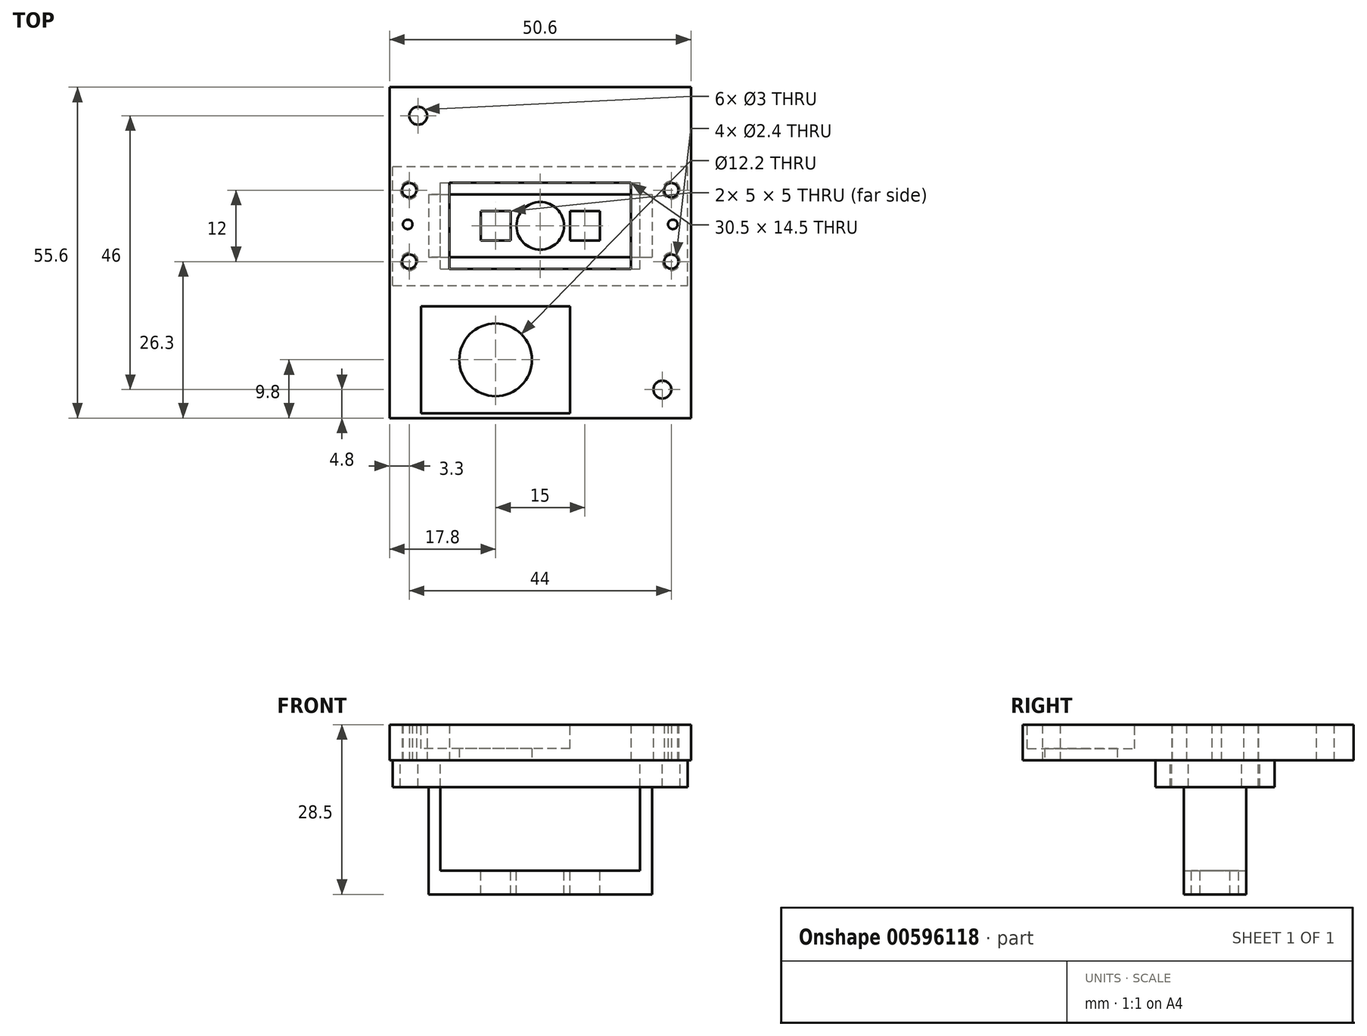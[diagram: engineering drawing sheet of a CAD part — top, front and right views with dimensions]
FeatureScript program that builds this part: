
annotation { "Feature Type Name" : "Feature", "Feature Type Description" : "" }
export const myFeature = defineFeature(function(context is Context, id is Id, definition is map)
    precondition{}
    {
        {
            var Q0;
            Q0=qCreatedBy(makeId("Top.planeOp"),FACE);
            var sketch = newSketch(context, id + "F0", { "sketchPlane" : qUnion([Q0])});
            skLineSegment(sketch, "E0.bottom", {"start": v(25.3, -27.8) * mm, "end": v(-25.3, -27.8) * mm});
            skLineSegment(sketch, "E0.top", {"start": v(25.3, 27.8) * mm, "end": v(-25.3, 27.8) * mm});
            skLineSegment(sketch, "E0.left", {"start": v(25.3, -27.8) * mm, "end": v(25.3, 27.8) * mm});
            skLineSegment(sketch, "E0.right", {"start": v(-25.3, -27.8) * mm, "end": v(-25.3, 27.8) * mm});
            skPoint(sketch, "E0.middle", {"position": v(0, 0) * mm});
            skLineSegment(sketch, "E1.bottom", {"start": v(15.25, -2.75) * mm, "end": v(-15.25, -2.75) * mm});
            skLineSegment(sketch, "E1.top", {"start": v(15.25, 11.75) * mm, "end": v(-15.25, 11.75) * mm});
            skLineSegment(sketch, "E1.left", {"start": v(15.25, -2.75) * mm, "end": v(15.25, 11.75) * mm});
            skLineSegment(sketch, "E1.right", {"start": v(-15.25, -2.75) * mm, "end": v(-15.25, 11.75) * mm});
            skPoint(sketch, "E1.middle", {"position": v(0, 4.5) * mm});
            skCircle(sketch, "E2", {"center": v(-20.5, 23) * mm, "radius": 1.5 * mm});
            skCircle(sketch, "E3", {"center": v(20.5, -23) * mm, "radius": 1.5 * mm});
            skCircle(sketch, "E4", {"center": v(-7.5, -18) * mm, "radius": 6.1 * mm});
            skCircle(sketch, "E5", {"center": v(22.25, 4.75) * mm, "radius": 0.8 * mm});
            skCircle(sketch, "E6", {"center": v(22, 10.5) * mm, "radius": 1.2 * mm});
            skCircle(sketch, "E7", {"center": v(22, -1.5) * mm, "radius": 1.2 * mm});
            skLineSegment(sketch, "E8", {"start": v(0, 4.5) * mm, "end": v(0, 17.43) * mm, "construction": true});
            skCircle(sketch, "E9.MirrorC", {"center": v(-22, -1.5) * mm, "radius": 1.2 * mm});
            skCircle(sketch, "E10.MirrorC", {"center": v(-22.25, 4.75) * mm, "radius": 0.8 * mm});
            skCircle(sketch, "E11.MirrorC", {"center": v(-22, 10.5) * mm, "radius": 1.2 * mm});
            skSolve(sketch);
        }
        {
            var Q0;
            Q0 = qSketchRegion(id + "F0", true);
            extrude(context, id + "F1", {"entities" : qUnion([Q0]), "depth" : 6 * mm, "offsetDistance" : 25 * mm});
        }
        {
            var Q0;
            Q0=makeQuery(id+"F1.opExtrude","CAP_FACE",FACE,{"disambiguationData":[OSD([sQuery(id+"F0.wireOp",EDGE,"E0.bottom"),sQuery(id+"F0.wireOp",EDGE,"E0.top"),sQuery(id+"F0.wireOp",EDGE,"E0.left"),sQuery(id+"F0.wireOp",EDGE,"E0.right"),sQuery(id+"F0.wireOp",EDGE,"E1.bottom"),sQuery(id+"F0.wireOp",EDGE,"E1.top"),sQuery(id+"F0.wireOp",EDGE,"E1.left"),sQuery(id+"F0.wireOp",EDGE,"E1.right"),sQuery(id+"F0.wireOp",EDGE,"E2"),sQuery(id+"F0.wireOp",EDGE,"E3"),sQuery(id+"F0.wireOp",EDGE,"E4"),sQuery(id+"F0.wireOp",EDGE,"vf1jpXBP-j2sW-oR5i-IoB6-HgW2j1TkzSlQ"),sQuery(id+"F0.wireOp",EDGE,"E5")])],"isStart":false});
            var sketch = newSketch(context, id + "F2", { "sketchPlane" : qUnion([Q0])});
            skLineSegment(sketch, "E12.bottom", {"start": v(5, -27) * mm, "end": v(-20, -27) * mm});
            skLineSegment(sketch, "E12.top", {"start": v(5, -9) * mm, "end": v(-20, -9) * mm});
            skLineSegment(sketch, "E12.left", {"start": v(5, -27) * mm, "end": v(5, -9) * mm});
            skLineSegment(sketch, "E12.right", {"start": v(-20, -27) * mm, "end": v(-20, -9) * mm});
            skPoint(sketch, "E12.middle", {"position": v(-7.5, -18) * mm});
            skSolve(sketch);
        }
        {
            var Q0;
            Q0 = qSketchRegion(id + "F2", true);
            extrude(context, id + "F3", {"entities" : qUnion([Q0]), "operationType" : NewBodyOperationType.REMOVE, "oppositeDirection" : true, "depth" : 4 * mm, "offsetDistance" : 25 * mm});
        }
        {
            var Q0;
            Q0=makeQuery(id+"F1.opExtrude","CAP_FACE",FACE,{"disambiguationData":[OSD([sQuery(id+"F0.wireOp",EDGE,"E0.bottom"),sQuery(id+"F0.wireOp",EDGE,"E0.top"),sQuery(id+"F0.wireOp",EDGE,"E0.left"),sQuery(id+"F0.wireOp",EDGE,"E0.right"),sQuery(id+"F0.wireOp",EDGE,"E1.bottom"),sQuery(id+"F0.wireOp",EDGE,"E1.top"),sQuery(id+"F0.wireOp",EDGE,"E1.left"),sQuery(id+"F0.wireOp",EDGE,"E1.right"),sQuery(id+"F0.wireOp",EDGE,"E2"),sQuery(id+"F0.wireOp",EDGE,"E3"),sQuery(id+"F0.wireOp",EDGE,"E4"),sQuery(id+"F0.wireOp",EDGE,"vf1jpXBP-j2sW-oR5i-IoB6-HgW2j1TkzSlQ"),sQuery(id+"F0.wireOp",EDGE,"E5")])],"isStart":true});
            var sketch = newSketch(context, id + "F4", { "sketchPlane" : qUnion([Q0])});
            skLineSegment(sketch, "E13.bottom", {"start": v(-16.75, 2.75) * mm, "end": v(16.75, 2.75) * mm});
            skLineSegment(sketch, "E13.top", {"start": v(-16.75, -11.75) * mm, "end": v(16.75, -11.75) * mm});
            skLineSegment(sketch, "E13.left", {"start": v(-16.75, 2.75) * mm, "end": v(-16.75, -11.75) * mm});
            skLineSegment(sketch, "E13.right", {"start": v(16.75, 2.75) * mm, "end": v(16.75, -11.75) * mm});
            skPoint(sketch, "E13.middle", {"position": v(0, -4.5) * mm});
            skPoint(sketch, "E13.middle.positionSnap0", {"position": v(15.25, -4.5) * mm});
            skPoint(sketch, "E13.middle.positionSnap1", {"position": v(0, -11.75) * mm});
            skPoint(sketch, "E13.centerSnap0", {"position": v(15.25, -4.5) * mm});
            skPoint(sketch, "E13.centerSnap1", {"position": v(0, -11.75) * mm});
            skLineSegment(sketch, "E14.bottom", {"start": v(-24.75, 5.5) * mm, "end": v(24.75, 5.5) * mm});
            skLineSegment(sketch, "E14.top", {"start": v(-24.75, -14.5) * mm, "end": v(24.75, -14.5) * mm});
            skLineSegment(sketch, "E14.left", {"start": v(-24.75, 5.5) * mm, "end": v(-24.75, -14.5) * mm});
            skLineSegment(sketch, "E14.right", {"start": v(24.75, 5.5) * mm, "end": v(24.75, -14.5) * mm});
            skCircle(sketch, "E15", {"center": v(22, -10.5) * mm, "radius": 1.5 * mm});
            skCircle(sketch, "E16", {"center": v(22, 1.5) * mm, "radius": 1.5 * mm});
            skLineSegment(sketch, "E17", {"start": v(0, -4.5) * mm, "end": v(0, -33.87) * mm, "construction": true});
            skCircle(sketch, "E18.MirrorC", {"center": v(-22, 1.5) * mm, "radius": 1.5 * mm});
            skCircle(sketch, "E19.MirrorC", {"center": v(-22, -10.5) * mm, "radius": 1.5 * mm});
            skSolve(sketch);
        }
        {
            var Q0;
            Q0 = qSketchRegion(id + "F4", true);
            extrude(context, id + "F5", {"entities" : qUnion([Q0]), "depth" : 4.5 * mm, "offsetDistance" : 25 * mm});
        }
        {
            var Q0;
            Q0=makeQuery(id+"F5.opExtrude","CAP_FACE",FACE,{"disambiguationData":[OSD([sQuery(id+"F4.wireOp",EDGE,"E13.bottom"),sQuery(id+"F4.wireOp",EDGE,"E13.top"),sQuery(id+"F4.wireOp",EDGE,"E13.left"),sQuery(id+"F4.wireOp",EDGE,"E13.right"),sQuery(id+"F4.wireOp",EDGE,"E14.bottom"),sQuery(id+"F4.wireOp",EDGE,"E14.top"),sQuery(id+"F4.wireOp",EDGE,"E14.left"),sQuery(id+"F4.wireOp",EDGE,"E14.right"),sQuery(id+"F4.wireOp",EDGE,"E15"),sQuery(id+"F4.wireOp",EDGE,"E16"),sQuery(id+"F4.wireOp",EDGE,"E18.MirrorC"),sQuery(id+"F4.wireOp",EDGE,"E19.MirrorC")])],"isStart":false});
            var sketch = newSketch(context, id + "F6", { "sketchPlane" : qUnion([Q0])});
            skLineSegment(sketch, "E20.bottom", {"start": v(16.75, -9.75) * mm, "end": v(18.75, -9.75) * mm});
            skLineSegment(sketch, "E20.top", {"start": v(16.75, 0.75) * mm, "end": v(18.75, 0.75) * mm});
            skLineSegment(sketch, "E20.left", {"start": v(16.75, -9.75) * mm, "end": v(16.75, 0.75) * mm});
            skLineSegment(sketch, "E20.right", {"start": v(18.75, -9.75) * mm, "end": v(18.75, 0.75) * mm});
            skLineSegment(sketch, "E21.bottom", {"start": v(-16.75, -9.75) * mm, "end": v(-18.75, -9.75) * mm});
            skLineSegment(sketch, "E21.top", {"start": v(-16.75, 0.75) * mm, "end": v(-18.75, 0.75) * mm});
            skLineSegment(sketch, "E21.left", {"start": v(-16.75, -9.75) * mm, "end": v(-16.75, 0.75) * mm});
            skLineSegment(sketch, "E21.right", {"start": v(-18.75, -9.75) * mm, "end": v(-18.75, 0.75) * mm});
            skSolve(sketch);
        }
        {
            var Q0;
            Q0 = qSketchRegion(id + "F6", true);
            extrude(context, id + "F7", {"entities" : qUnion([Q0]), "operationType" : NewBodyOperationType.ADD, "depth" : 14 * mm, "offsetDistance" : 25 * mm});
        }
        {
            var Q0;
            Q0=makeQuery(id+"F7.opExtrude","CAP_FACE",FACE,{"disambiguationData":[OSD([sQuery(id+"F6.wireOp",EDGE,"E20.bottom"),sQuery(id+"F6.wireOp",EDGE,"E20.top"),sQuery(id+"F6.wireOp",EDGE,"E20.left"),sQuery(id+"F6.wireOp",EDGE,"E20.right")])],"isStart":false});
            var sketch = newSketch(context, id + "F8", { "sketchPlane" : qUnion([Q0])});
            skCircle(sketch, "E22", {"center": v(0, -4.5) * mm, "radius": 4 * mm});
            skLineSegment(sketch, "E23.bottom", {"start": v(-5, -7) * mm, "end": v(-10, -7) * mm});
            skLineSegment(sketch, "E23.top", {"start": v(-5, -2) * mm, "end": v(-10, -2) * mm});
            skLineSegment(sketch, "E23.left", {"start": v(-5, -7) * mm, "end": v(-5, -2) * mm});
            skLineSegment(sketch, "E23.right", {"start": v(-10, -7) * mm, "end": v(-10, -2) * mm});
            skPoint(sketch, "E23.middle", {"position": v(-7.5, -4.5) * mm});
            skLineSegment(sketch, "E24.bottom", {"start": v(10, -7) * mm, "end": v(5, -7) * mm});
            skLineSegment(sketch, "E24.top", {"start": v(10, -2) * mm, "end": v(5, -2) * mm});
            skLineSegment(sketch, "E24.left", {"start": v(10, -7) * mm, "end": v(10, -2) * mm});
            skLineSegment(sketch, "E24.right", {"start": v(5, -7) * mm, "end": v(5, -2) * mm});
            skPoint(sketch, "E24.middle", {"position": v(7.5, -4.5) * mm});
            skLineSegment(sketch, "E25.bottom", {"start": v(-18.75, -9.75) * mm, "end": v(18.75, -9.75) * mm});
            skLineSegment(sketch, "E25.top", {"start": v(-18.75, 0.75) * mm, "end": v(18.75, 0.75) * mm});
            skLineSegment(sketch, "E25.left", {"start": v(-18.75, -9.75) * mm, "end": v(-18.75, 0.75) * mm});
            skLineSegment(sketch, "E25.right", {"start": v(18.75, -9.75) * mm, "end": v(18.75, 0.75) * mm});
            skSolve(sketch);
        }
        {
            var Q0;
            Q0 = qSketchRegion(id + "F8", true);
            extrude(context, id + "F9", {"entities" : qUnion([Q0]), "operationType" : NewBodyOperationType.ADD, "depth" : 4 * mm, "offsetDistance" : 25 * mm});
        }
    });
